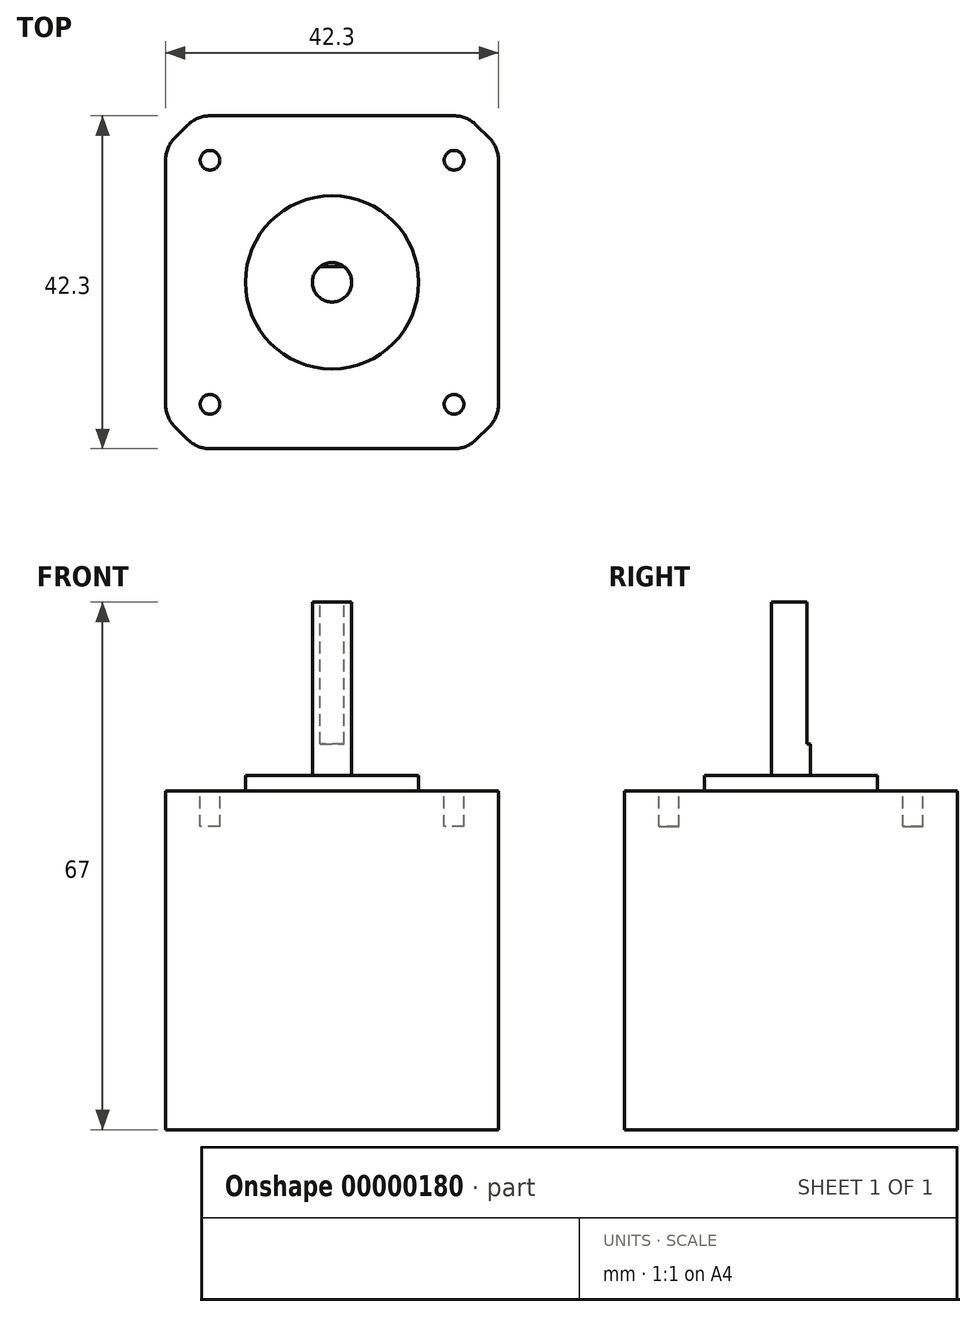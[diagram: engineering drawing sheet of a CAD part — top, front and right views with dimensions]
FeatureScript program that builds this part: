
annotation { "Feature Type Name" : "Feature", "Feature Type Description" : "" }
export const myFeature = defineFeature(function(context is Context, id is Id, definition is map)
    precondition{}
    {
        {
            var Q0;
            Q0=qCreatedBy(makeId("Top.planeOp"),FACE);
            var sketch = newSketch(context, id + "F0", { "sketchPlane" : qUnion([Q0])});
            skLineSegment(sketch, "E0.bottom", {"start": v(-21.15, 21.15) * mm, "end": v(21.15, 21.15) * mm});
            skLineSegment(sketch, "E0.top", {"start": v(-21.15, -21.15) * mm, "end": v(21.15, -21.15) * mm});
            skLineSegment(sketch, "E0.left", {"start": v(-21.15, 21.15) * mm, "end": v(-21.15, -21.15) * mm});
            skLineSegment(sketch, "E0.right", {"start": v(21.15, 21.15) * mm, "end": v(21.15, -21.15) * mm});
            skLineSegment(sketch, "E1", {"start": v(-21.15, 21.15) * mm, "end": v(21.15, -21.15) * mm, "construction": true});
            skSolve(sketch);
        }
        {
            var Q0;
            Q0=makeQuery(id+"F0.imprint","IMPRINT",FACE,{"disambiguationData":[TD([[makeQuery(id+"F0.imprint","IMPRINT",EDGE,{"derivedFrom":sQuery(id+"F0.wireOp",EDGE,"E0.bottom")}),-1.0]])]});
            extrude(context, id + "F1", {"entities" : qUnion([Q0]), "depth" : 43 * mm});
        }
        {
            var Q0;
            Q0=makeQuery(id+"F1.opExtrude","CAP_FACE",FACE,{"disambiguationData":[OSD([sQuery(id+"F0.wireOp",EDGE,"E0.bottom"),sQuery(id+"F0.wireOp",EDGE,"E0.top"),sQuery(id+"F0.wireOp",EDGE,"E0.left"),sQuery(id+"F0.wireOp",EDGE,"E0.right")])],"isStart":false});
            var sketch = newSketch(context, id + "F2", { "sketchPlane" : qUnion([Q0])});
            skCircle(sketch, "E2", {"center": v(0, 0) * mm, "radius": 11 * mm});
            skSolve(sketch);
        }
        {
            var Q0;
            Q0=makeQuery(id+"F2.imprint","IMPRINT",FACE,{"disambiguationData":[TD([[makeQuery(id+"F2.imprint","IMPRINT",EDGE,{"derivedFrom":sQuery(id+"F2.wireOp",EDGE,"E2")}),1.0]])]});
            extrude(context, id + "F3", {"entities" : qUnion([Q0]), "operationType" : NewBodyOperationType.ADD, "depth" : 2 * mm});
        }
        {
            var Q0;
            Q0=makeQuery(id+"F1.opExtrude","CAP_FACE",FACE,{"disambiguationData":[OSD([sQuery(id+"F0.wireOp",EDGE,"E0.bottom"),sQuery(id+"F0.wireOp",EDGE,"E0.top"),sQuery(id+"F0.wireOp",EDGE,"E0.left"),sQuery(id+"F0.wireOp",EDGE,"E0.right")])],"isStart":false});
            var sketch = newSketch(context, id + "F4", { "sketchPlane" : qUnion([Q0])});
            skLineSegment(sketch, "E3.bottom", {"start": v(-15.5, 15.5) * mm, "end": v(15.5, 15.5) * mm, "construction": true});
            skLineSegment(sketch, "E3.top", {"start": v(-15.5, -15.5) * mm, "end": v(15.5, -15.5) * mm, "construction": true});
            skLineSegment(sketch, "E3.left", {"start": v(-15.5, 15.5) * mm, "end": v(-15.5, -15.5) * mm, "construction": true});
            skLineSegment(sketch, "E3.right", {"start": v(15.5, 15.5) * mm, "end": v(15.5, -15.5) * mm, "construction": true});
            skLineSegment(sketch, "E4", {"start": v(-15.5, 15.5) * mm, "end": v(15.5, -15.5) * mm, "construction": true});
            skCircle(sketch, "E5", {"center": v(-15.5, 15.5) * mm, "radius": 1.25 * mm});
            skCircle(sketch, "E6", {"center": v(15.5, 15.5) * mm, "radius": 1.25 * mm});
            skCircle(sketch, "E7", {"center": v(15.5, -15.5) * mm, "radius": 1.25 * mm});
            skCircle(sketch, "E8", {"center": v(-15.5, -15.5) * mm, "radius": 1.25 * mm});
            skSolve(sketch);
        }
        {
            var Q0;
            {Q0=qUnion([makeQuery(id+"F4.imprint","IMPRINT",FACE,{"disambiguationData":[TD([[makeQuery(id+"F4.imprint","IMPRINT",EDGE,{"derivedFrom":sQuery(id+"F4.wireOp",EDGE,"E5")}),1.0]])]}),makeQuery(id+"F4.imprint","IMPRINT",FACE,{"disambiguationData":[TD([[makeQuery(id+"F4.imprint","IMPRINT",EDGE,{"derivedFrom":sQuery(id+"F4.wireOp",EDGE,"E6")}),1.0]])]}),makeQuery(id+"F4.imprint","IMPRINT",FACE,{"disambiguationData":[TD([[makeQuery(id+"F4.imprint","IMPRINT",EDGE,{"derivedFrom":sQuery(id+"F4.wireOp",EDGE,"E7")}),1.0]])]}),makeQuery(id+"F4.imprint","IMPRINT",FACE,{"disambiguationData":[TD([[makeQuery(id+"F4.imprint","IMPRINT",EDGE,{"derivedFrom":sQuery(id+"F4.wireOp",EDGE,"E8")}),1.0]])]})]);}
            extrude(context, id + "F5", {"entities" : qUnion([Q0]), "operationType" : NewBodyOperationType.REMOVE, "oppositeDirection" : true, "depth" : 4.5 * mm});
        }
        {
            var Q0;
            Q0=makeQuery(id+"F1.opExtrude","SWEPT_EDGE",EDGE,{"disambiguationData":[OSD([sQuery(id+"F0.wireOp",EDGE,"E0.bottom"),sQuery(id+"F0.wireOp",EDGE,"E0.left")])]});
            var Q1;
            Q1=makeQuery(id+"F1.opExtrude","SWEPT_EDGE",EDGE,{"disambiguationData":[OSD([sQuery(id+"F0.wireOp",EDGE,"E0.bottom"),sQuery(id+"F0.wireOp",EDGE,"E0.right")])]});
            var Q2;
            Q2=makeQuery(id+"F1.opExtrude","SWEPT_EDGE",EDGE,{"disambiguationData":[OSD([sQuery(id+"F0.wireOp",EDGE,"E0.top"),sQuery(id+"F0.wireOp",EDGE,"E0.right")])]});
            var Q3;
            Q3=makeQuery(id+"F1.opExtrude","SWEPT_EDGE",EDGE,{"disambiguationData":[OSD([sQuery(id+"F0.wireOp",EDGE,"E0.top"),sQuery(id+"F0.wireOp",EDGE,"E0.left")])]});
            chamfer(context, id + "F6", {"entities" : qUnion([Q0, Q1, Q2, Q3]), "width" : 4 * mm, "tangentPropagation" : true});
        }
        {
            var Q0;
            {var subQ0=sQuery(id+"F0.wireOp",EDGE,"E0.left");Q0=makeQuery(id+"F6.opChamfer","BLEND_EDGE",EDGE,{"blendedFrom":[makeQuery(id+"F1.opExtrude","SWEPT_EDGE",EDGE,{"disambiguationData":[OSD([sQuery(id+"F0.wireOp",EDGE,"E0.bottom"),subQ0])]}),makeQuery(id+"F1.opExtrude","SWEPT_FACE",FACE,{"disambiguationData":[OSD([subQ0])]})],"blendedInto":[makeQuery(id+"F1.opExtrude","SWEPT_FACE",FACE,{"disambiguationData":[OSD([subQ0])]})]});}
            var Q1;
            {var subQ0=sQuery(id+"F0.wireOp",EDGE,"E0.bottom");Q1=makeQuery(id+"F6.opChamfer","BLEND_EDGE",EDGE,{"blendedFrom":[makeQuery(id+"F1.opExtrude","SWEPT_EDGE",EDGE,{"disambiguationData":[OSD([subQ0,sQuery(id+"F0.wireOp",EDGE,"E0.left")])]}),makeQuery(id+"F1.opExtrude","SWEPT_FACE",FACE,{"disambiguationData":[OSD([subQ0])]})],"blendedInto":[makeQuery(id+"F1.opExtrude","SWEPT_FACE",FACE,{"disambiguationData":[OSD([subQ0])]})]});}
            var Q2;
            {var subQ0=sQuery(id+"F0.wireOp",EDGE,"E0.bottom");Q2=makeQuery(id+"F6.opChamfer","BLEND_EDGE",EDGE,{"blendedFrom":[makeQuery(id+"F1.opExtrude","SWEPT_EDGE",EDGE,{"disambiguationData":[OSD([subQ0,sQuery(id+"F0.wireOp",EDGE,"E0.right")])]}),makeQuery(id+"F1.opExtrude","SWEPT_FACE",FACE,{"disambiguationData":[OSD([subQ0])]})],"blendedInto":[makeQuery(id+"F1.opExtrude","SWEPT_FACE",FACE,{"disambiguationData":[OSD([subQ0])]})]});}
            var Q3;
            {var subQ0=sQuery(id+"F0.wireOp",EDGE,"E0.right");Q3=makeQuery(id+"F6.opChamfer","BLEND_EDGE",EDGE,{"blendedFrom":[makeQuery(id+"F1.opExtrude","SWEPT_EDGE",EDGE,{"disambiguationData":[OSD([sQuery(id+"F0.wireOp",EDGE,"E0.bottom"),subQ0])]}),makeQuery(id+"F1.opExtrude","SWEPT_FACE",FACE,{"disambiguationData":[OSD([subQ0])]})],"blendedInto":[makeQuery(id+"F1.opExtrude","SWEPT_FACE",FACE,{"disambiguationData":[OSD([subQ0])]})]});}
            var Q4;
            {var subQ0=sQuery(id+"F0.wireOp",EDGE,"E0.left");Q4=makeQuery(id+"F6.opChamfer","BLEND_EDGE",EDGE,{"blendedFrom":[makeQuery(id+"F1.opExtrude","SWEPT_EDGE",EDGE,{"disambiguationData":[OSD([sQuery(id+"F0.wireOp",EDGE,"E0.top"),subQ0])]}),makeQuery(id+"F1.opExtrude","SWEPT_FACE",FACE,{"disambiguationData":[OSD([subQ0])]})],"blendedInto":[makeQuery(id+"F1.opExtrude","SWEPT_FACE",FACE,{"disambiguationData":[OSD([subQ0])]})]});}
            var Q5;
            {var subQ0=sQuery(id+"F0.wireOp",EDGE,"E0.top");Q5=makeQuery(id+"F6.opChamfer","BLEND_EDGE",EDGE,{"blendedFrom":[makeQuery(id+"F1.opExtrude","SWEPT_EDGE",EDGE,{"disambiguationData":[OSD([subQ0,sQuery(id+"F0.wireOp",EDGE,"E0.left")])]}),makeQuery(id+"F1.opExtrude","SWEPT_FACE",FACE,{"disambiguationData":[OSD([subQ0])]})],"blendedInto":[makeQuery(id+"F1.opExtrude","SWEPT_FACE",FACE,{"disambiguationData":[OSD([subQ0])]})]});}
            var Q6;
            {var subQ0=sQuery(id+"F0.wireOp",EDGE,"E0.top");Q6=makeQuery(id+"F6.opChamfer","BLEND_EDGE",EDGE,{"blendedFrom":[makeQuery(id+"F1.opExtrude","SWEPT_EDGE",EDGE,{"disambiguationData":[OSD([subQ0,sQuery(id+"F0.wireOp",EDGE,"E0.right")])]}),makeQuery(id+"F1.opExtrude","SWEPT_FACE",FACE,{"disambiguationData":[OSD([subQ0])]})],"blendedInto":[makeQuery(id+"F1.opExtrude","SWEPT_FACE",FACE,{"disambiguationData":[OSD([subQ0])]})]});}
            var Q7;
            {var subQ0=sQuery(id+"F0.wireOp",EDGE,"E0.right");Q7=makeQuery(id+"F6.opChamfer","BLEND_EDGE",EDGE,{"blendedFrom":[makeQuery(id+"F1.opExtrude","SWEPT_EDGE",EDGE,{"disambiguationData":[OSD([sQuery(id+"F0.wireOp",EDGE,"E0.top"),subQ0])]}),makeQuery(id+"F1.opExtrude","SWEPT_FACE",FACE,{"disambiguationData":[OSD([subQ0])]})],"blendedInto":[makeQuery(id+"F1.opExtrude","SWEPT_FACE",FACE,{"disambiguationData":[OSD([subQ0])]})]});}
            fillet(context, id + "F7", {"entities" : qUnion([Q0, Q1, Q2, Q3, Q4, Q5, Q6, Q7]), "radius" : 4 * mm, "tangentPropagation" : true, "allowEdgeOverflow" : false});
        }
        {
            var Q0;
            Q0=makeQuery(id+"F3.opExtrude","CAP_FACE",FACE,{"disambiguationData":[OSD([sQuery(id+"F2.wireOp",EDGE,"E2")])],"isStart":false});
            var sketch = newSketch(context, id + "F8", { "sketchPlane" : qUnion([Q0])});
            skCircle(sketch, "E9", {"center": v(0, 0) * mm, "radius": 2.5 * mm});
            skSolve(sketch);
        }
        {
            var Q0;
            Q0=makeQuery(id+"F8.imprint","IMPRINT",FACE,{"disambiguationData":[TD([[makeQuery(id+"F8.imprint","IMPRINT",EDGE,{"derivedFrom":sQuery(id+"F8.wireOp",EDGE,"E9")}),1.0]])]});
            extrude(context, id + "F9", {"entities" : qUnion([Q0]), "operationType" : NewBodyOperationType.ADD, "depth" : 22 * mm});
        }
        {
            var Q0;
            Q0=makeQuery(id+"F9.opExtrude","CAP_FACE",FACE,{"disambiguationData":[OSD([sQuery(id+"F8.wireOp",EDGE,"E9")])],"isStart":false});
            var sketch = newSketch(context, id + "F10", { "sketchPlane" : qUnion([Q0])});
            skArc(sketch, "E10", {"start": v(1.5, 2) * mm, "mid": v(0, 2.5) * mm, "end": v(-1.5, 2) * mm});
            skLineSegment(sketch, "E11", {"start": v(-1.5, 2) * mm, "end": v(1.5, 2) * mm});
            skSolve(sketch);
        }
        {
            var Q0;
            Q0=makeQuery(id+"F10.imprint","IMPRINT",FACE,{"disambiguationData":[TD([[makeQuery(id+"F10.imprint","IMPRINT",EDGE,{"derivedFrom":sQuery(id+"F10.wireOp",EDGE,"E10")}),1.0]])]});
            extrude(context, id + "F11", {"entities" : qUnion([Q0]), "operationType" : NewBodyOperationType.REMOVE, "oppositeDirection" : true, "depth" : 18 * mm});
        }
    });
